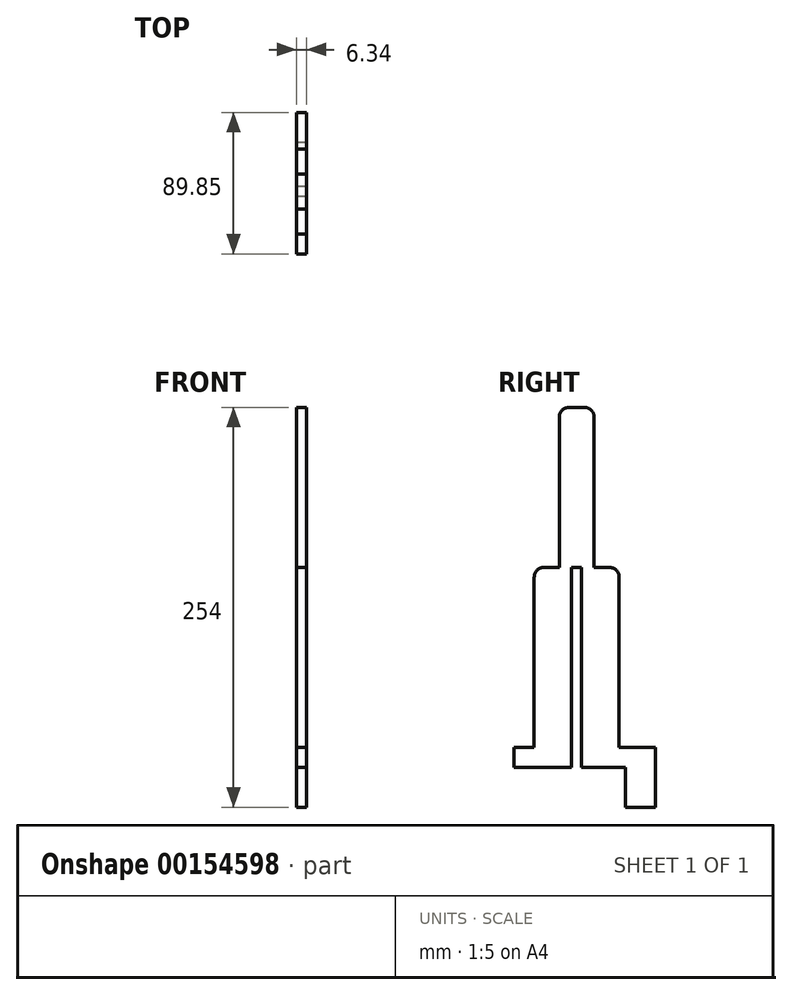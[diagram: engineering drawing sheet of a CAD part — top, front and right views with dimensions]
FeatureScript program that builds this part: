
annotation { "Feature Type Name" : "Feature", "Feature Type Description" : "" }
export const myFeature = defineFeature(function(context is Context, id is Id, definition is map)
    precondition{}
    {
        {
            var Q0;
            Q0=qCreatedBy(makeId("Right.planeOp"),FACE);
            var sketch = newSketch(context, id + "F0", { "sketchPlane" : qUnion([Q0])});
            skLineSegment(sketch, "E0.bottom", {"start": v(26.99, -63.5) * mm, "end": v(3.18, -63.5) * mm});
            skLineSegment(sketch, "E0.top", {"start": v(20.64, 63.5) * mm, "end": v(17.46, 63.5) * mm});
            skLineSegment(sketch, "E0.left", {"start": v(26.99, -63.5) * mm, "end": v(26.99, 57.15) * mm});
            skLineSegment(sketch, "E0.right", {"start": v(-26.99, -63.5) * mm, "end": v(-26.99, 57.15) * mm});
            skPoint(sketch, "E0.middle", {"position": v(0, 0) * mm});
            skLineSegment(sketch, "E1", {"start": v(-11.1, 63.5) * mm, "end": v(-11.1, 158.75) * mm});
            skLineSegment(sketch, "E2", {"start": v(-4.75, 165.1) * mm, "end": v(4.77, 165.1) * mm});
            skLineSegment(sketch, "E3", {"start": v(11.12, 158.75) * mm, "end": v(11.11, 63.5) * mm});
            skLineSegment(sketch, "E4.trimOffspring", {"start": v(-17.45, 63.5) * mm, "end": v(-20.64, 63.5) * mm});
            skPoint(sketch, "E5.start.orphan", {"position": v(0, -63.5) * mm});
            skPoint(sketch, "E6.visualSharp", {"position": v(-11.1, 63.5) * mm});
            skPoint(sketch, "E7.visualSharp", {"position": v(11.11, 63.5) * mm});
            skPoint(sketch, "E8.visualSharp", {"position": v(-26.99, 63.5) * mm});
            skArc(sketch, "E8.filletArc", {"start": v(-20.64, 63.5) * mm, "mid": v(-25.13, 61.64) * mm, "end": v(-26.99, 57.15) * mm});
            skPoint(sketch, "E9.visualSharp", {"position": v(26.99, 63.5) * mm});
            skArc(sketch, "E9.filletArc", {"start": v(26.99, 57.15) * mm, "mid": v(25.13, 61.64) * mm, "end": v(20.64, 63.5) * mm});
            skPoint(sketch, "E10.visualSharp", {"position": v(11.13, 165.1) * mm});
            skArc(sketch, "E10.filletArc", {"start": v(11.12, 158.75) * mm, "mid": v(9.26, 163.24) * mm, "end": v(4.77, 165.1) * mm});
            skPoint(sketch, "E11.visualSharp", {"position": v(-11.1, 165.1) * mm});
            skArc(sketch, "E11.filletArc", {"start": v(-4.75, 165.1) * mm, "mid": v(-9.24, 163.24) * mm, "end": v(-11.1, 158.75) * mm});
            skLineSegment(sketch, "E12", {"start": v(-3.18, -63.5) * mm, "end": v(-3.18, 63.5) * mm});
            skLineSegment(sketch, "E13", {"start": v(-3.18, 63.5) * mm, "end": v(3.17, 63.5) * mm});
            skLineSegment(sketch, "E14", {"start": v(3.17, 63.5) * mm, "end": v(3.17, -63.5) * mm});
            skLineSegment(sketch, "E15.trimOffspring", {"start": v(-3.18, -63.5) * mm, "end": v(-26.99, -63.5) * mm});
            skLineSegment(sketch, "E16", {"start": v(-17.45, 63.5) * mm, "end": v(-11.1, 63.5) * mm});
            skLineSegment(sketch, "E17", {"start": v(11.11, 63.5) * mm, "end": v(17.46, 63.5) * mm});
            skLineSegment(sketch, "E18", {"start": v(3.18, -63.5) * mm, "end": v(31.12, -63.5) * mm});
            skLineSegment(sketch, "E19", {"start": v(31.12, -63.5) * mm, "end": v(31.12, -88.9) * mm});
            skLineSegment(sketch, "E20", {"start": v(31.12, -88.9) * mm, "end": v(50.17, -88.9) * mm});
            skLineSegment(sketch, "E21", {"start": v(50.17, -88.9) * mm, "end": v(50.17, -50.8) * mm});
            skLineSegment(sketch, "E22", {"start": v(50.17, -50.8) * mm, "end": v(26.99, -50.8) * mm});
            skLineSegment(sketch, "E23", {"start": v(26.99, -50.8) * mm, "end": v(26.99, -63.5) * mm});
            skLineSegment(sketch, "E24", {"start": v(-26.99, -63.5) * mm, "end": v(-26.99, -50.82) * mm});
            skLineSegment(sketch, "E25", {"start": v(-26.99, -50.82) * mm, "end": v(-39.69, -50.82) * mm});
            skLineSegment(sketch, "E26", {"start": v(-39.69, -50.82) * mm, "end": v(-39.69, -63.52) * mm});
            skLineSegment(sketch, "E27", {"start": v(-39.69, -63.52) * mm, "end": v(-26.99, -63.5) * mm});
            skSolve(sketch);
        }
        {
            var Q0;
            Q0=qSketchRegion(id+"F0",true);
            extrude(context, id + "F1", {"entities" : qUnion([Q0]), "endBound" : BoundingType.SYMMETRIC, "depth" : 6.35 * mm});
        }
    });
